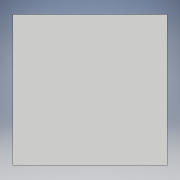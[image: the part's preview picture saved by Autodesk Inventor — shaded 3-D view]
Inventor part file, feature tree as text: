
AUTODESK INVENTOR PART (.ipt)
format: ipt  version: 2018.2 (Build 222227000, 227)  size: 80,896 bytes
history: native  units: mm
features: other x1, extrude x1, sketch x1
ambient origin geometry x8: Origin, YZ Plane, XZ Plane, XY Plane, X Axis, Y Axis, Z Axis, Center Point
bodies: Body1 (feature_tree)
feature tree (3):
  other  "ソリッド1"
  extrude  "押し出し1"  Depth=6000.0mm
  sketch  "スケッチ1"
